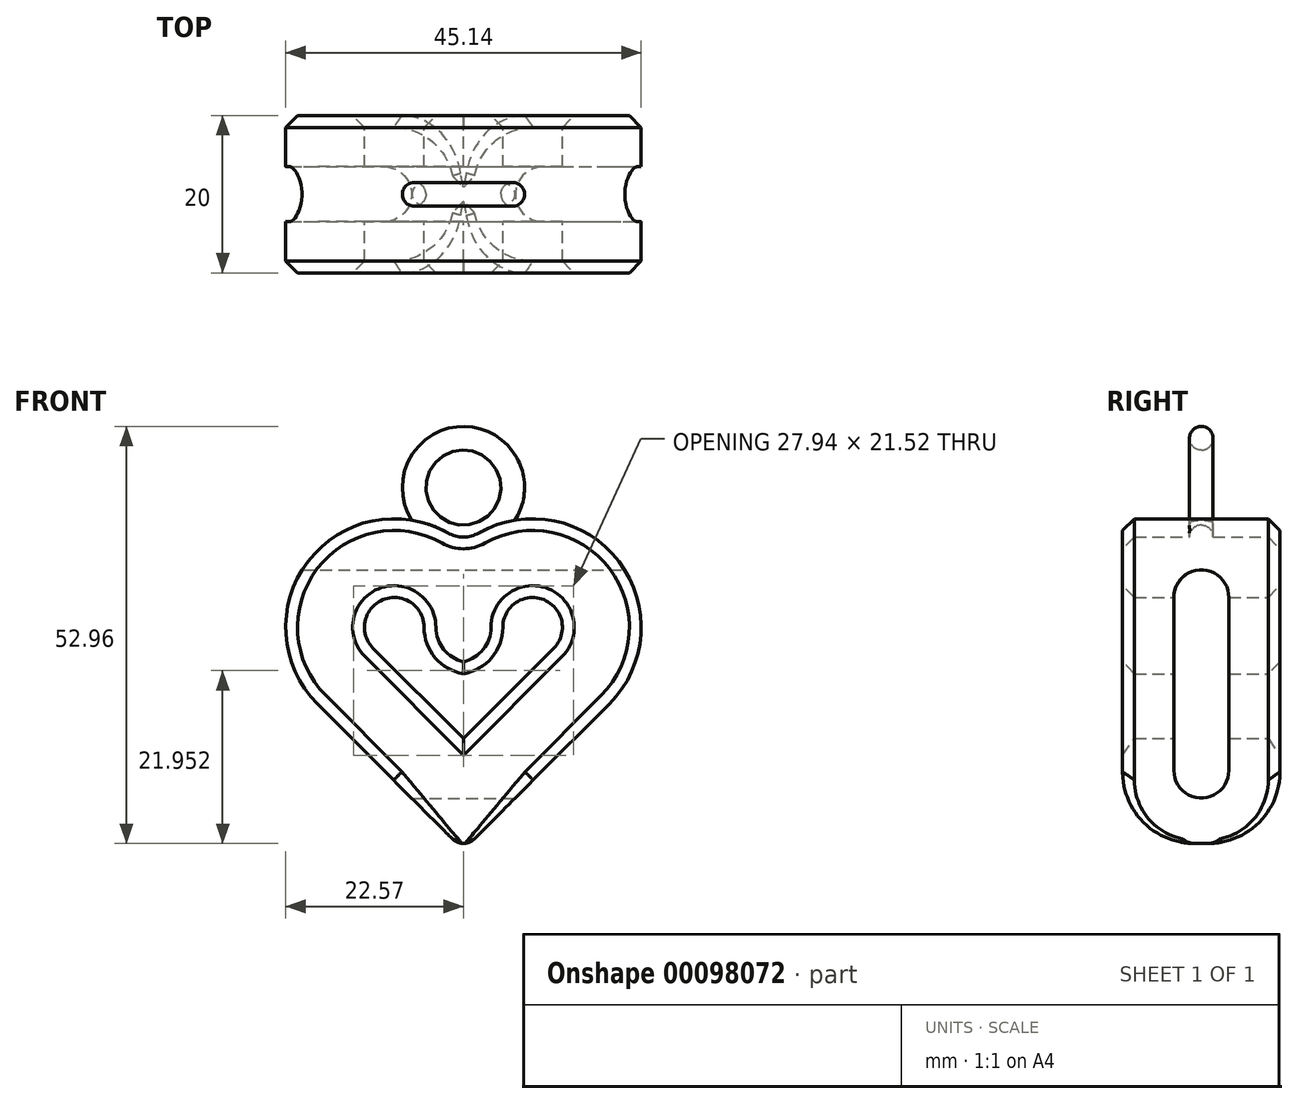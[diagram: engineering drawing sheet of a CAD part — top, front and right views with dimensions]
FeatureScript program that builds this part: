
annotation { "Feature Type Name" : "Feature", "Feature Type Description" : "" }
export const myFeature = defineFeature(function(context is Context, id is Id, definition is map)
    precondition{}
    {
        {
            var Q0;
            Q0=qCreatedBy(makeId("Front.planeOp"),FACE);
            var sketch = newSketch(context, id + "F0", { "sketchPlane" : qUnion([Q0])});
            skLineSegment(sketch, "E0", {"start": v(0, 15) * mm, "end": v(0, -15) * mm, "construction": true});
            skLineSegment(sketch, "E1", {"start": v(0, 0) * mm, "end": v(-49.93, 0) * mm, "construction": true});
            skLineSegment(sketch, "E2", {"start": v(0, -15) * mm, "end": v(-15, 0) * mm, "construction": true});
            skLineSegment(sketch, "E3", {"start": v(0, 15) * mm, "end": v(-49.93, 15) * mm, "construction": true});
            skArc(sketch, "E4", {"start": v(0, 6.21) * mm, "mid": v(-12.15, 14.33) * mm, "end": v(-15, 0) * mm, "construction": true});
            skLineSegment(sketch, "E5.0", {"start": v(-1.41, -20.66) * mm, "end": v(-18.54, -3.54) * mm});
            skArc(sketch, "E5.1", {"start": v(-1.98, 18.2) * mm, "mid": v(-19.75, 14.57) * mm, "end": v(-18.54, -3.54) * mm});
            skLineSegment(sketch, "E6.0", {"start": v(0, -7.93) * mm, "end": v(-11.46, 3.54) * mm});
            skArc(sketch, "E6.1", {"start": v(-5, 6.21) * mm, "mid": v(-10.24, 9.71) * mm, "end": v(-11.46, 3.54) * mm});
            skArc(sketch, "E7", {"start": v(-5, 6.21) * mm, "mid": v(-3.58, 2.34) * mm, "end": v(0, 0.3) * mm});
            skArc(sketch, "E8.MirrorCS", {"start": v(1.98, 18.2) * mm, "mid": v(19.75, 14.57) * mm, "end": v(18.54, -3.54) * mm});
            skArc(sketch, "E9.MirrorCS", {"start": v(5, 6.21) * mm, "mid": v(10.24, 9.71) * mm, "end": v(11.46, 3.54) * mm});
            skLineSegment(sketch, "E10.MirrorCS", {"start": v(0, -7.93) * mm, "end": v(11.46, 3.54) * mm});
            skLineSegment(sketch, "E11.MirrorCS", {"start": v(1.41, -20.66) * mm, "end": v(18.54, -3.54) * mm});
            skArc(sketch, "E12.MirrorCS", {"start": v(5, 6.21) * mm, "mid": v(3.58, 2.34) * mm, "end": v(0, 0.3) * mm});
            skLineSegment(sketch, "E13", {"start": v(-5, 6.21) * mm, "end": v(0, 6.21) * mm, "construction": true});
            skPoint(sketch, "E14.visualSharp", {"position": v(0, 16.84) * mm});
            skArc(sketch, "E14.filletArc", {"start": v(-1.98, 18.2) * mm, "mid": v(0, 17.68) * mm, "end": v(1.98, 18.2) * mm});
            skPoint(sketch, "E15.visualSharp", {"position": v(0, -22.07) * mm});
            skArc(sketch, "E15.filletArc", {"start": v(-1.41, -20.66) * mm, "mid": v(0, -21.24) * mm, "end": v(1.41, -20.66) * mm});
            skSolve(sketch);
        }
        {
            var Q0;
            Q0=qSketchRegion(id+"F0",true);
            extrude(context, id + "F1", {"entities" : qUnion([Q0]), "endBound" : BoundingType.SYMMETRIC, "depth" : 20 * mm});
        }
        {
            var Q0;
            Q0=qCreatedBy(makeId("Right.planeOp"),FACE);
            var sketch = newSketch(context, id + "F2", { "sketchPlane" : qUnion([Q0])});
            skLineSegment(sketch, "E16.0", {"start": v(-10, -21.24) * mm, "end": v(-10, -20.66) * mm, "construction": true});
            skLineSegment(sketch, "E16.1", {"start": v(10, -21.24) * mm, "end": v(10, -20.66) * mm, "construction": true});
            skLineSegment(sketch, "E16.2", {"start": v(10, -20.66) * mm, "end": v(10, -3.54) * mm, "construction": true});
            skLineSegment(sketch, "E16.3", {"start": v(-10, -20.66) * mm, "end": v(-10, -3.54) * mm, "construction": true});
            skLineSegment(sketch, "E16.4", {"start": v(-10, -3.54) * mm, "end": v(10, -3.54) * mm, "construction": true});
            skLineSegment(sketch, "E17", {"start": v(-10, -21.24) * mm, "end": v(10, -21.24) * mm, "construction": true});
            skLineSegment(sketch, "E18", {"start": v(0, -21.24) * mm, "end": v(0, -3.54) * mm, "construction": true});
            skArc(sketch, "E19", {"start": v(-10, -12.14) * mm, "mid": v(-7.33, -18.58) * mm, "end": v(-0.9, -21.24) * mm});
            skLineSegment(sketch, "E20", {"start": v(-0.9, -21.24) * mm, "end": v(-10, -21.24) * mm});
            skLineSegment(sketch, "E21", {"start": v(-10, -12.14) * mm, "end": v(-10, -21.24) * mm});
            skArc(sketch, "E22.MirrorCS", {"start": v(10, -12.14) * mm, "mid": v(7.33, -18.58) * mm, "end": v(0.9, -21.24) * mm});
            skLineSegment(sketch, "E23.MirrorCS", {"start": v(10, -12.14) * mm, "end": v(10, -21.24) * mm});
            skLineSegment(sketch, "E24.MirrorCS", {"start": v(0.9, -21.24) * mm, "end": v(10, -21.24) * mm});
            skSolve(sketch);
        }
        {
            var Q0;
            Q0=qSketchRegion(id+"F2",true);
            extrude(context, id + "F3", {"entities" : qUnion([Q0]), "operationType" : NewBodyOperationType.REMOVE, "endBound" : BoundingType.SYMMETRIC, "depth" : 25 * mm});
        }
        {
            var Q0;
            Q0=makeQuery(id+"F1.opExtrude","CAP_FACE",FACE,{"disambiguationData":[OSD([sQuery(id+"F0.wireOp",EDGE,"E5.0"),sQuery(id+"F0.wireOp",EDGE,"E5.1"),sQuery(id+"F0.wireOp",EDGE,"E6.0"),sQuery(id+"F0.wireOp",EDGE,"E6.1"),sQuery(id+"F0.wireOp",EDGE,"E7"),sQuery(id+"F0.wireOp",EDGE,"E8.MirrorCS"),sQuery(id+"F0.wireOp",EDGE,"E9.MirrorCS"),sQuery(id+"F0.wireOp",EDGE,"E10.MirrorCS"),sQuery(id+"F0.wireOp",EDGE,"E11.MirrorCS"),sQuery(id+"F0.wireOp",EDGE,"E12.MirrorCS"),sQuery(id+"F0.wireOp",EDGE,"E14.filletArc"),sQuery(id+"F0.wireOp",EDGE,"E15.filletArc")])],"isStart":false});
            var Q1;
            Q1=makeQuery(id+"F1.opExtrude","CAP_FACE",FACE,{"disambiguationData":[OSD([sQuery(id+"F0.wireOp",EDGE,"E5.0"),sQuery(id+"F0.wireOp",EDGE,"E5.1"),sQuery(id+"F0.wireOp",EDGE,"E6.0"),sQuery(id+"F0.wireOp",EDGE,"E6.1"),sQuery(id+"F0.wireOp",EDGE,"E7"),sQuery(id+"F0.wireOp",EDGE,"E8.MirrorCS"),sQuery(id+"F0.wireOp",EDGE,"E9.MirrorCS"),sQuery(id+"F0.wireOp",EDGE,"E10.MirrorCS"),sQuery(id+"F0.wireOp",EDGE,"E11.MirrorCS"),sQuery(id+"F0.wireOp",EDGE,"E12.MirrorCS"),sQuery(id+"F0.wireOp",EDGE,"E14.filletArc"),sQuery(id+"F0.wireOp",EDGE,"E15.filletArc")])],"isStart":true});
            chamfer(context, id + "F4", {"entities" : qUnion([Q0, Q1]), "width" : 1.5 * mm, "tangentPropagation" : true});
        }
        {
            var Q0;
            Q0=qCreatedBy(makeId("Right.planeOp"),FACE);
            var sketch = newSketch(context, id + "F5", { "sketchPlane" : qUnion([Q0])});
            skLineSegment(sketch, "E25.0", {"start": v(-8.5, 20) * mm, "end": v(-8.5, -3.54) * mm, "construction": true});
            skLineSegment(sketch, "E25.1", {"start": v(-8.5, -3.54) * mm, "end": v(-8.5, -13.2) * mm, "construction": true});
            skLineSegment(sketch, "E25.2", {"start": v(8.5, -13.2) * mm, "end": v(8.5, -3.54) * mm, "construction": true});
            skLineSegment(sketch, "E25.3", {"start": v(8.5, -3.54) * mm, "end": v(8.5, 20) * mm, "construction": true});
            skLineSegment(sketch, "E26", {"start": v(-8.5, 20) * mm, "end": v(8.5, 20) * mm, "construction": true});
            skLineSegment(sketch, "E27", {"start": v(-8.5, -13.2) * mm, "end": v(8.5, -13.2) * mm, "construction": true});
            skLineSegment(sketch, "E28", {"start": v(-3.5, 10) * mm, "end": v(-3.5, -12) * mm});
            skLineSegment(sketch, "E29", {"start": v(3.5, 10) * mm, "end": v(3.5, -12) * mm});
            skArc(sketch, "E30", {"start": v(-3.5, -12) * mm, "mid": v(0, -15.5) * mm, "end": v(3.5, -12) * mm});
            skArc(sketch, "E31", {"start": v(3.5, 10) * mm, "mid": v(0, 13.5) * mm, "end": v(-3.5, 10) * mm});
            skLineSegment(sketch, "E32", {"start": v(3.5, -1) * mm, "end": v(8.5, -1) * mm, "construction": true});
            skLineSegment(sketch, "E33", {"start": v(-3.5, -1) * mm, "end": v(-8.5, -1) * mm, "construction": true});
            skSolve(sketch);
        }
        {
            var Q0;
            Q0=qSketchRegion(id+"F5",true);
            extrude(context, id + "F6", {"entities" : qUnion([Q0]), "operationType" : NewBodyOperationType.REMOVE, "endBound" : BoundingType.SYMMETRIC, "oppositeDirection" : true, "depth" : 70 * mm});
        }
        {
            var Q0;
            Q0=qCreatedBy(makeId("Right.planeOp"),FACE);
            var sketch = newSketch(context, id + "F7", { "sketchPlane" : qUnion([Q0])});
            skLineSegment(sketch, "E34.0.0", {"start": v(-3.5, -3.54) * mm, "end": v(-3.5, 10) * mm, "construction": true});
            skArc(sketch, "E34.0.1", {"start": v(-3.5, 10) * mm, "mid": v(0, 13.5) * mm, "end": v(3.5, 10) * mm, "construction": true});
            skLineSegment(sketch, "E34.0.2", {"start": v(3.5, 10) * mm, "end": v(3.5, -3.54) * mm, "construction": true});
            skLineSegment(sketch, "E34.0.3", {"start": v(3.5, -3.54) * mm, "end": v(8.5, -3.54) * mm, "construction": true});
            skLineSegment(sketch, "E34.0.4", {"start": v(8.5, -3.54) * mm, "end": v(8.5, 20) * mm, "construction": true});
            skLineSegment(sketch, "E34.0.5", {"start": v(8.5, 18.2) * mm, "end": v(-8.5, 18.2) * mm, "construction": true});
            skLineSegment(sketch, "E34.0.6", {"start": v(-8.5, 20) * mm, "end": v(-8.5, -3.54) * mm, "construction": true});
            skLineSegment(sketch, "E34.0.7", {"start": v(-8.5, -3.54) * mm, "end": v(-3.5, -3.54) * mm, "construction": true});
            skLineSegment(sketch, "E35", {"start": v(-8.5, 20) * mm, "end": v(8.5, 20) * mm, "construction": true});
            skCircle(sketch, "E36", {"center": v(0, 17.7) * mm, "radius": 1.5 * mm});
            skPoint(sketch, "E37", {"position": v(0, 20) * mm});
            skLineSegment(sketch, "E38", {"start": v(0, 19.2) * mm, "end": v(0, 17.7) * mm});
            skLineSegment(sketch, "E39", {"start": v(0, 17.7) * mm, "end": v(-2.05, 17.7) * mm, "construction": true});
            skLineSegment(sketch, "E40", {"start": v(0, 17.7) * mm, "end": v(0, 16.2) * mm, "construction": true});
            skSolve(sketch);
        }
        {
            var Q0;
            Q0=qCreatedBy(makeId("Front.planeOp"),FACE);
            var sketch = newSketch(context, id + "F8", { "sketchPlane" : qUnion([Q0])});
            skCircle(sketch, "E41", {"center": v(0, 23.96) * mm, "radius": 10 * mm});
            skSolve(sketch);
        }
        {
            var Q0;
            Q0=makeQuery(id+"F7.imprint","IMPRINT",FACE,{"disambiguationData":[TD([[makeQuery(id+"F7.imprint","IMPRINT",EDGE,{"derivedFrom":sQuery(id+"F7.wireOp",EDGE,"E36")}),1.0]])]});
            var Q1;
            Q1=sQuery(id+"F8.wireOp",EDGE,"E41");
            revolve(context, id + "F9", {"operationType" : NewBodyOperationType.ADD, "entities" : qUnion([Q0]), "axis" : qUnion([Q1]), "revolveType" : RevolveType.FULL});
        }
    });
